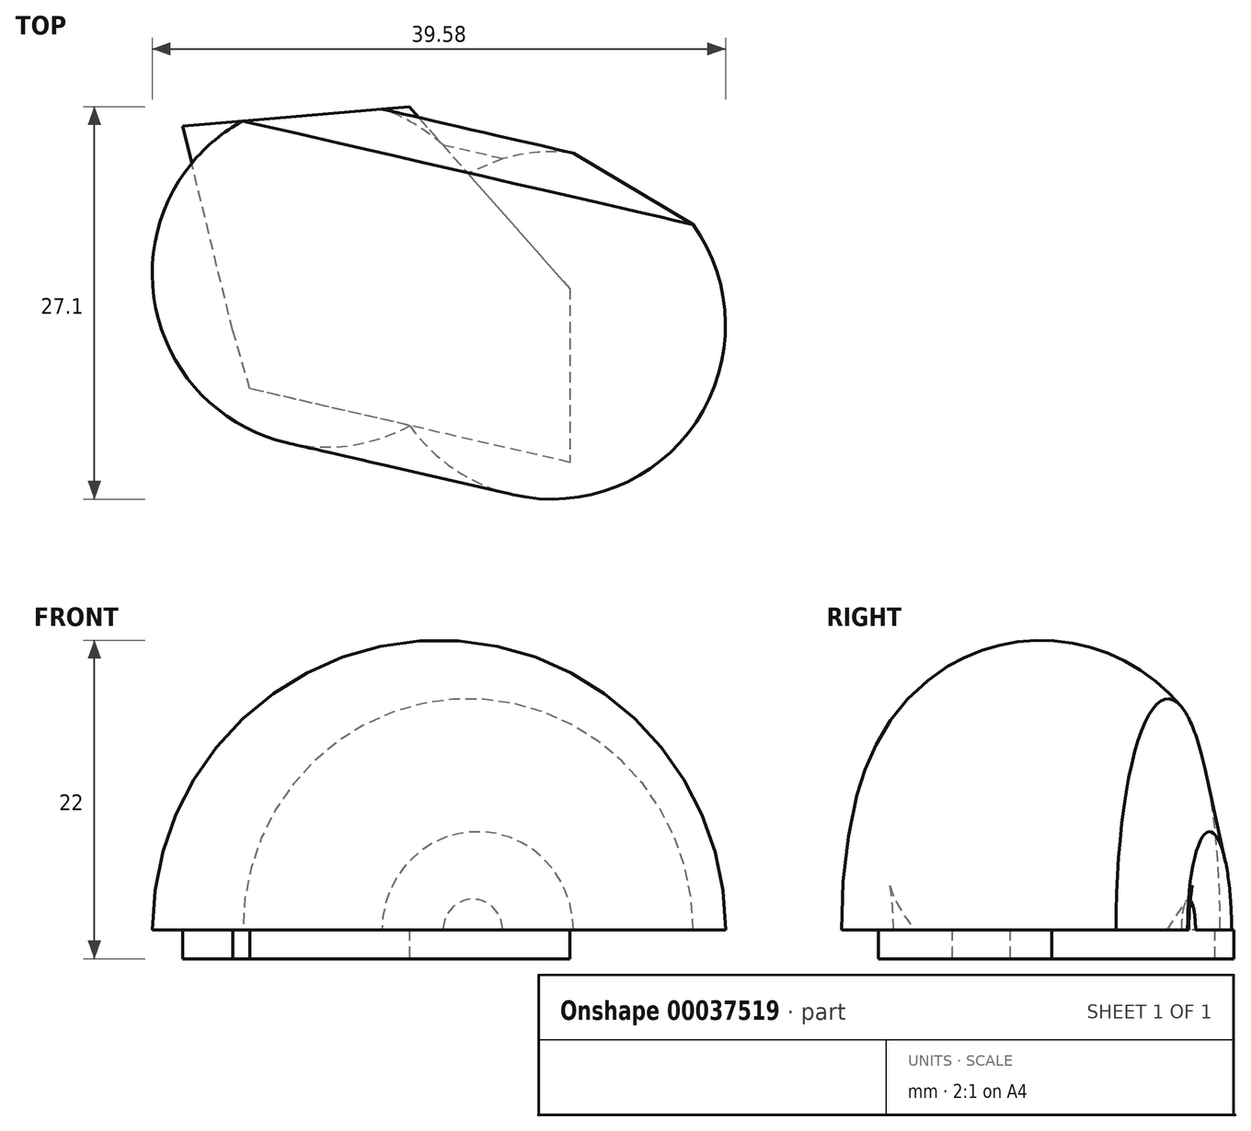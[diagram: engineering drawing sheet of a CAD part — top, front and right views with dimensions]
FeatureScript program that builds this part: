
annotation { "Feature Type Name" : "Feature", "Feature Type Description" : "" }
export const myFeature = defineFeature(function(context is Context, id is Id, definition is map)
    precondition{}
    {
        {
            var Q0;
            Q0=qCreatedBy(makeId("Top.planeOp"),FACE);
            var sketch = newSketch(context, id + "F0", { "sketchPlane" : qUnion([Q0])});
            skLineSegment(sketch, "E0", {"start": v(-23.26, 9.09) * mm, "end": v(-26.73, 23.22) * mm});
            skLineSegment(sketch, "E1", {"start": v(-26.73, 23.22) * mm, "end": v(-11.09, 24.56) * mm});
            skLineSegment(sketch, "E2", {"start": v(-11.09, 24.56) * mm, "end": v(0, 12) * mm});
            skLineSegment(sketch, "E3", {"start": v(0, 12) * mm, "end": v(0, 0) * mm});
            skLineSegment(sketch, "E4", {"start": v(0, 0) * mm, "end": v(-22.08, 5.08) * mm});
            skLineSegment(sketch, "E5", {"start": v(-22.08, 5.08) * mm, "end": v(-23.26, 9.09) * mm});
            skSolve(sketch);
        }
        {
            var Q0;
            Q0 = qSketchRegion(id + "F0", true);
            extrude(context, id + "F1", {"entities" : qUnion([Q0]), "endBound" : BoundingType.SYMMETRIC, "depth" : 2 * mm});
        }
        {
            var Q0;
            Q0=makeQuery(id+"F1.opExtrude","CAP_FACE",FACE,{"disambiguationData":[OSD([sQuery(id+"F0.wireOp",EDGE,"E0"),sQuery(id+"F0.wireOp",EDGE,"E1"),sQuery(id+"F0.wireOp",EDGE,"E2"),sQuery(id+"F0.wireOp",EDGE,"E3"),sQuery(id+"F0.wireOp",EDGE,"E4"),sQuery(id+"F0.wireOp",EDGE,"E5")])],"isStart":false});
            var sketch = newSketch(context, id + "F2", { "sketchPlane" : qUnion([Q0])});
            skArc(sketch, "E6", {"start": v(-7.03, 19.96) * mm, "mid": v(-28.52, 15.74) * mm, "end": v(-11.04, 2.54) * mm});
            skLineSegment(sketch, "E7", {"start": v(-11.04, 2.54) * mm, "end": v(-7.03, 19.96) * mm});
            skSolve(sketch);
        }
        {
            var Q0;
            {var subQ2=sQuery(id+"F2.wireOp",EDGE,"E7");Q0=makeQuery(id+"F2.imprint","IMPRINT",FACE,{"disambiguationData":[TD([[makeQuery(id+"F2.imprint","IMPRINT",EDGE,{"derivedFrom":subQ2}),1.0]])]});}
            var Q1;
            {var subQ3=makeQuery(id+"F1.opExtrude","CAP_EDGE",EDGE,{"disambiguationData":[OSD([sQuery(id+"F0.wireOp",EDGE,"E5")])],"isStart":false});Q1=makeQuery(id+"F2.imprint","IMPRINT",FACE,{"disambiguationData":[TD([[makeQuery(id+"F2.imprint","IMPRINT",EDGE,{"derivedFrom":subQ3}),1.0]])]});}
            var Q2;
            Q2=sQuery(id+"F2.wireOp",EDGE,"E7");
            revolve(context, id + "F3", {"operationType" : NewBodyOperationType.ADD, "entities" : qUnion([Q0, Q1]), "axis" : qUnion([Q2]), "revolveType" : RevolveType.ONE_DIRECTION, "angle" : 180 * degree});
        }
    });
